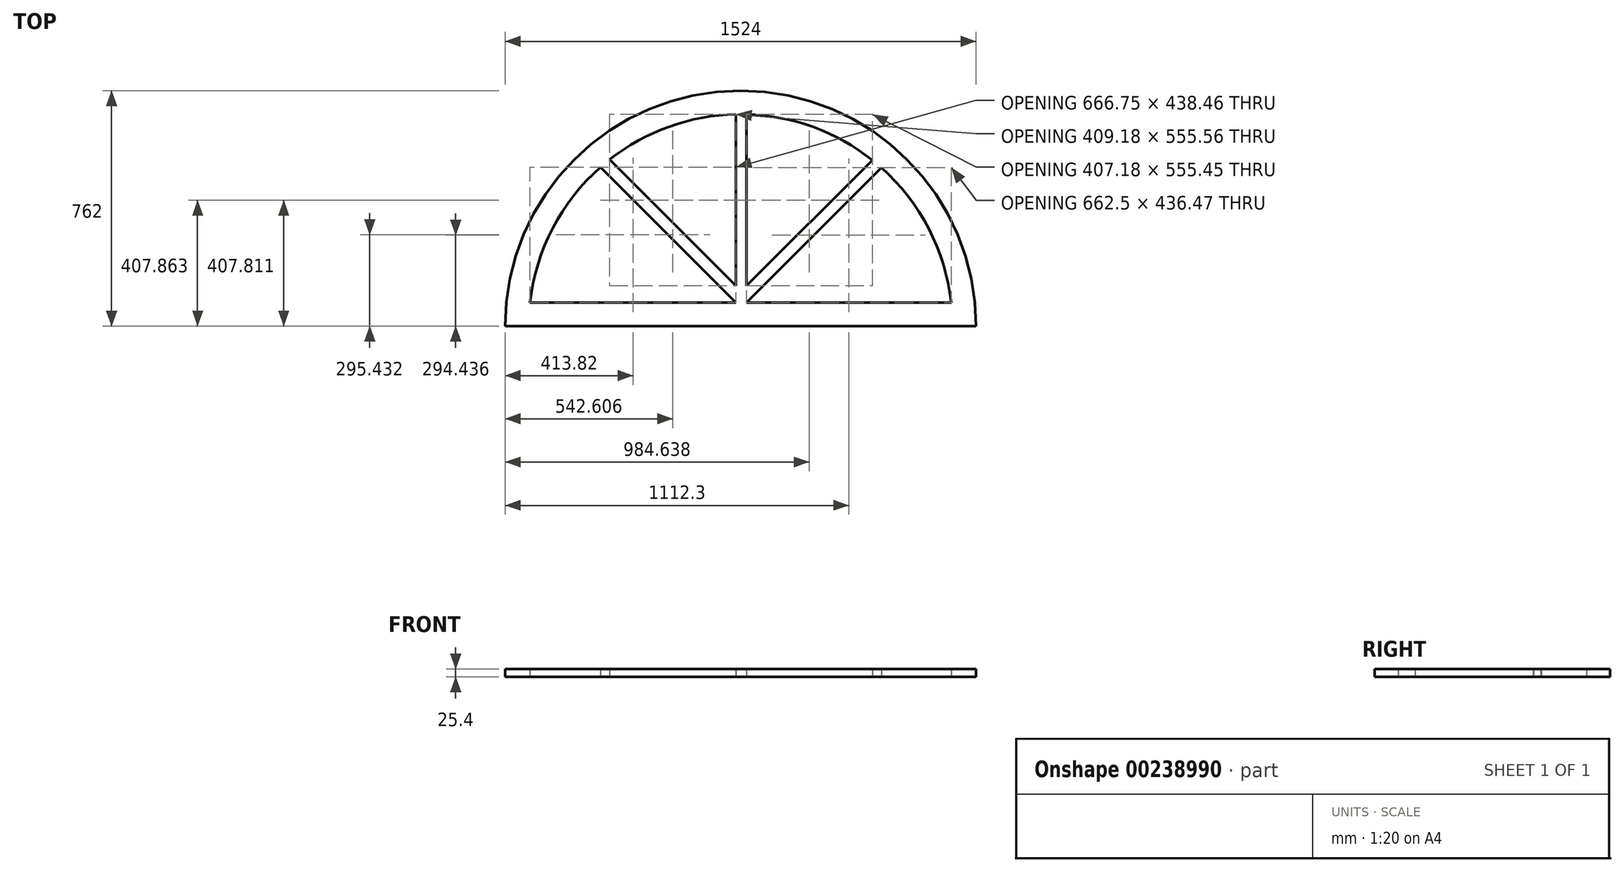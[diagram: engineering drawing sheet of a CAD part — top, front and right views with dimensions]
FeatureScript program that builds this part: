
annotation { "Feature Type Name" : "Feature", "Feature Type Description" : "" }
export const myFeature = defineFeature(function(context is Context, id is Id, definition is map)
    precondition{}
    {
        {
            var Q0;
            Q0=qCreatedBy(makeId("Top.planeOp"),FACE);
            var sketch = newSketch(context, id + "F0", { "sketchPlane" : qUnion([Q0])});
            skLineSegment(sketch, "E0", {"start": v(-168.28, -48.78) * mm, "end": v(1355.72, -48.78) * mm});
            skLineSegment(sketch, "E1", {"start": v(-168.28, -48.78) * mm, "end": v(593.72, -48.78) * mm});
            skLineSegment(sketch, "E2", {"start": v(1355.72, -48.78) * mm, "end": v(1355.72, -48.78) * mm});
            skLineSegment(sketch, "E3", {"start": v(593.72, 713.22) * mm, "end": v(593.72, 713.22) * mm});
            skLineSegment(sketch, "E4", {"start": v(-168.28, -48.78) * mm, "end": v(-168.28, -48.78) * mm});
            skPoint(sketch, "E5.visualSharp", {"position": v(1355.72, 713.22) * mm});
            skPoint(sketch, "E6.visualSharp", {"position": v(-168.28, 713.22) * mm});
            skArc(sketch, "E6.filletArc", {"start": v(593.72, 713.22) * mm, "mid": v(54.9, 490.04) * mm, "end": v(-168.28, -48.78) * mm});
            skArc(sketch, "E7.filletArc", {"start": v(1355.72, -48.78) * mm, "mid": v(1132.53, 490.04) * mm, "end": v(593.72, 713.22) * mm});
            skPoint(sketch, "E8.start.orphan", {"position": v(1279.52, 27.42) * mm});
            skPoint(sketch, "E9.end.orphan", {"position": v(1279.52, -48.78) * mm});
            skArc(sketch, "E10", {"start": v(1275.27, 27.42) * mm, "mid": v(1202.7, 266.6) * mm, "end": v(1049.23, 463.89) * mm});
            skLineSegment(sketch, "E11", {"start": v(612.77, 27.42) * mm, "end": v(1279.52, 27.42) * mm});
            skPoint(sketch, "E12.endSnap0", {"position": v(1049.48, 27.42) * mm});
            skPoint(sketch, "E13.trimOffspring.end.orphan", {"position": v(-209.62, 27.42) * mm});
            skLineSegment(sketch, "E14.trimOffspring", {"start": v(1279.52, 27.42) * mm, "end": v(612.77, 27.42) * mm});
            skPoint(sketch, "E15.trimOffspring.end.orphan", {"position": v(1521.02, 27.42) * mm});
            skLineSegment(sketch, "E16", {"start": v(612.77, 27.42) * mm, "end": v(1049.23, 463.89) * mm});
            skLineSegment(sketch, "E17", {"start": v(917.77, 386.3) * mm, "end": v(1019.95, 488.48) * mm});
            skLineSegment(sketch, "E18", {"start": v(1019.95, 488.48) * mm, "end": v(612.77, 81.3) * mm});
            skArc(sketch, "E19.trimOffspring", {"start": v(1019.95, 488.48) * mm, "mid": v(828.38, 595.63) * mm, "end": v(612.77, 636.76) * mm});
            skLineSegment(sketch, "E20", {"start": v(612.77, 81.3) * mm, "end": v(612.77, 636.76) * mm});
            skPoint(sketch, "E21.orphan", {"position": v(558.89, 27.42) * mm});
            skLineSegment(sketch, "E22.trimOffspring", {"start": v(558.89, 27.42) * mm, "end": v(-87.83, 27.42) * mm});
            skPoint(sketch, "E23.orphan", {"position": v(577.94, 27.42) * mm});
            skLineSegment(sketch, "E24", {"start": v(-87.83, 27.42) * mm, "end": v(578.92, 27.42) * mm});
            skLineSegment(sketch, "E25", {"start": v(578.92, 27.42) * mm, "end": v(140.46, 465.88) * mm});
            skLineSegment(sketch, "E26", {"start": v(386.57, 273.54) * mm, "end": v(386.63, 273.6) * mm});
            skLineSegment(sketch, "E27", {"start": v(578.92, 81.3) * mm, "end": v(578.92, 636.86) * mm});
            skLineSegment(sketch, "E28", {"start": v(169.74, 490.26) * mm, "end": v(578.92, 81.3) * mm});
            skArc(sketch, "E29.trimOffspring", {"start": v(140.46, 465.88) * mm, "mid": v(-14.57, 267.94) * mm, "end": v(-87.83, 27.42) * mm});
            skPoint(sketch, "E30.orphan", {"position": v(359.69, 246.65) * mm});
            skArc(sketch, "E31.trimOffspring", {"start": v(578.92, 636.86) * mm, "mid": v(362.4, 596.83) * mm, "end": v(169.74, 490.26) * mm});
            skSolve(sketch);
        }
        {
            var Q0;
            Q0 = qSketchRegion(id + "F0", true);
            extrude(context, id + "F1", {"entities" : qUnion([Q0]), "depth" : 25.4 * mm});
        }
    });
